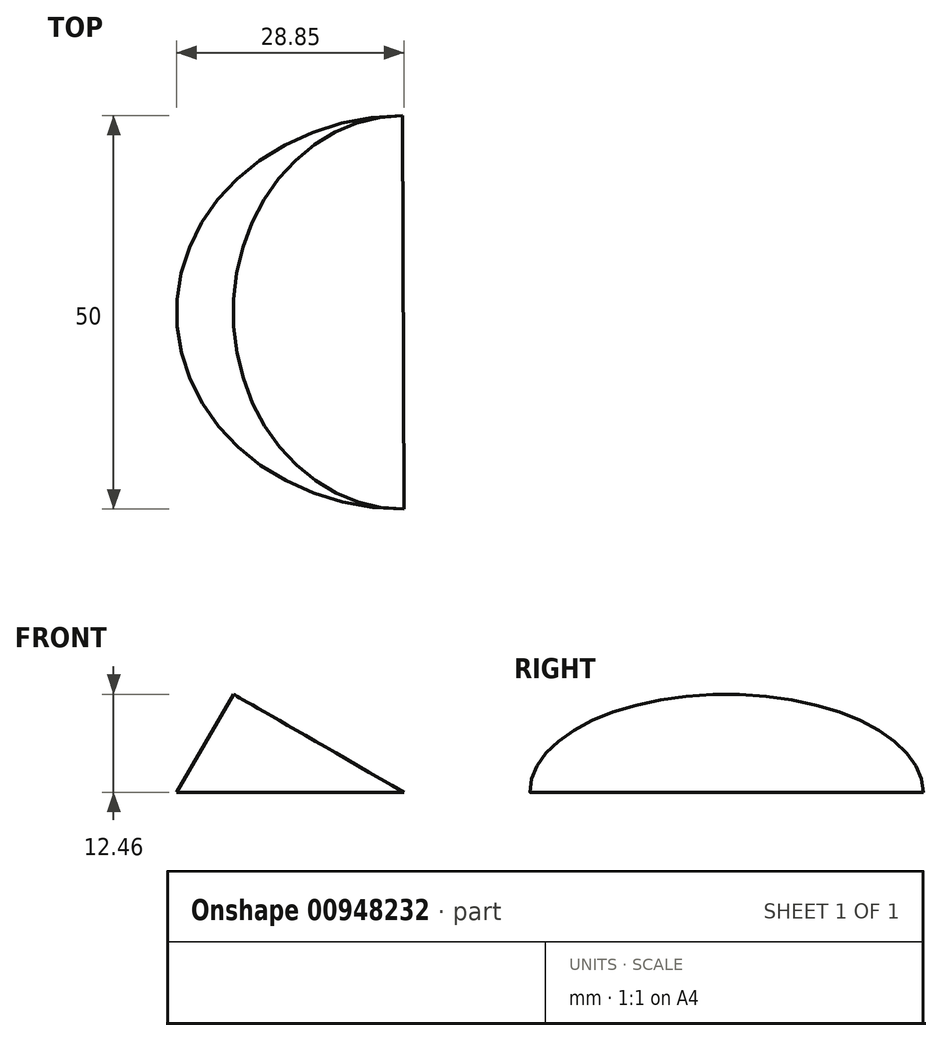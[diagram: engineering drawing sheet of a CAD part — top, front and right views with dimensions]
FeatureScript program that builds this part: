
annotation { "Feature Type Name" : "Feature", "Feature Type Description" : "" }
export const myFeature = defineFeature(function(context is Context, id is Id, definition is map)
    precondition{}
    {
        {
            var Q0;
            Q0=qCreatedBy(makeId("Top.planeOp"),FACE);
            var sketch = newSketch(context, id + "F0", { "sketchPlane" : qUnion([Q0])});
            skCircle(sketch, "E0", {"center": v(0, 0) * mm, "radius": 41 * mm, "construction": true});
            skArc(sketch, "E1", {"start": v(-0.16, 11) * mm, "mid": v(-25, -14.08) * mm, "end": v(0, -39) * mm});
            skLineSegment(sketch, "E2", {"start": v(0, -14) * mm, "end": v(0, 0) * mm, "construction": true});
            skLineSegment(sketch, "E3", {"start": v(0, -14) * mm, "end": v(0, 0) * mm});
            skLineSegment(sketch, "E4", {"start": v(-0.16, 11) * mm, "end": v(0, -39) * mm});
            skSolve(sketch);
        }
        {
            var Q0;
            Q0=makeQuery(id+"F0.imprint","IMPRINT",FACE,{"disambiguationData":[TD([[makeQuery(id+"F0.imprint","IMPRINT",EDGE,{"derivedFrom":sQuery(id+"F0.wireOp",EDGE,"E1")}),1.0]])]});
            var Q1;
            Q1=sQuery(id+"F0.wireOp",EDGE,"E4");
            revolve(context, id + "F1", {"surfaceOperationType" : NewSurfaceOperationType.NEW, "entities" : qUnion([Q0]), "axis" : qUnion([Q1]), "revolveType" : RevolveType.ONE_DIRECTION, "oppositeDirection" : true, "angle" : 30 * degree});
        }
        {
            var Q0;
            Q0=makeQuery(id+"F1.opRevolve","CAP_FACE",FACE,{"disambiguationData":[OSD([sQuery(id+"F0.wireOp",EDGE,"E1"),sQuery(id+"F0.wireOp",EDGE,"E4")])],"isStart":false});
            var sketch = newSketch(context, id + "F2", { "sketchPlane" : qUnion([Q0])});
            skArc(sketch, "E5", {"start": v(-0.15, 11) * mm, "mid": v(-24.98, -14.1) * mm, "end": v(0.04, -39) * mm});
            skLineSegment(sketch, "E6", {"start": v(0.04, -39) * mm, "end": v(-0.15, 11) * mm});
            skSolve(sketch);
        }
        {
            var Q0;
            Q0 = qSketchRegion(id + "F2", true);
            var Q1;
            Q1=makeQuery(id+"F1.opRevolve","CAP_FACE",FACE,{"disambiguationData":[OSD([sQuery(id+"F0.wireOp",EDGE,"E1"),sQuery(id+"F0.wireOp",EDGE,"E4")])],"isStart":true});
            extrude(context, id + "F3", {"entities" : qUnion([Q0]), "operationType" : NewBodyOperationType.ADD, "endBound" : BoundingType.UP_TO_SURFACE, "oppositeDirection" : true, "depth" : 25 * mm, "endBoundEntityFace" : qUnion([Q1]), "offsetDistance" : 25 * mm});
        }
    });
